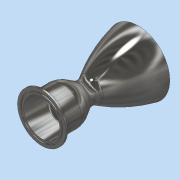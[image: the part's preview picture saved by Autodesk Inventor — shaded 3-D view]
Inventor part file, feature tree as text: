
AUTODESK INVENTOR PART (.ipt)
format: ipt  version: 2020 (Build 240168000, 168)  size: 240,128 bytes
history: native  units: in
note: dims shown in document units (in); Inventor stores cm internally (conversion verified against a paired STEP export)
features: fillet x4, other x2
ambient origin geometry x8: Origin, YZ Plane, XZ Plane, XY Plane, X Axis, Y Axis, Z Axis, Center Point
bodies: Body1 (feature_tree)
feature tree (6):
  other  "CD Nozzle"
  fillet  "Fillet14"  [1 undecoded]
  fillet  "Fillet15"  Radius=1.7717in
  fillet  "Fillet16"  Radius=1.378in
  fillet  "Fillet17"  Radius=0.5906in
  other  "CD Nozzle Sketch"
note: 1 required parameter value undecoded (feature->parameter linkage not recoverable at this tier; creation-order binding heuristic only, values carry confidence <= 0.55)
